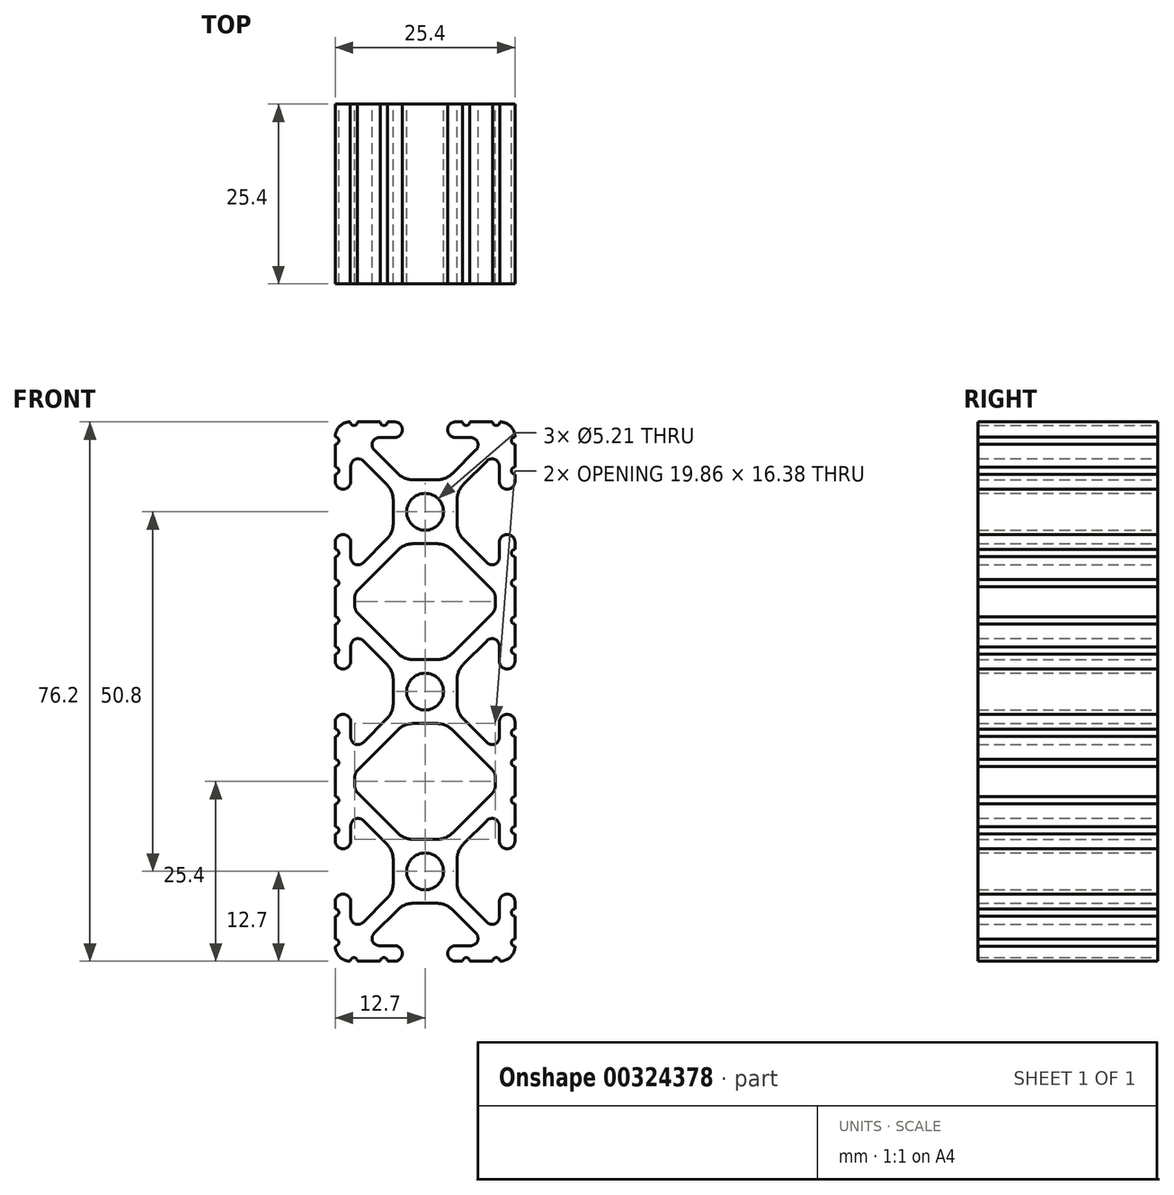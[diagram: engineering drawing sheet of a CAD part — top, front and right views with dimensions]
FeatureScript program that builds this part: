
annotation { "Feature Type Name" : "Feature", "Feature Type Description" : "" }
export const myFeature = defineFeature(function(context is Context, id is Id, definition is map)
    precondition{}
    {
        {
            var Q0;
            Q0=qCreatedBy(makeId("Front.planeOp"),FACE);
            var sketch = newSketch(context, id + "F0", { "sketchPlane" : qUnion([Q0])});
            skArc(sketch, "E0", {"start": v(2.6, 25.4) * mm, "mid": v(0, 28) * mm, "end": v(-2.6, 25.4) * mm});
            skArc(sketch, "E1", {"start": v(-2.6, 25.4) * mm, "mid": v(0, 22.8) * mm, "end": v(2.6, 25.4) * mm});
            skArc(sketch, "E2", {"start": v(-10.57, 38.1) * mm, "mid": v(-10.06, 37.6) * mm, "end": v(-9.55, 38.1) * mm});
            skArc(sketch, "E3", {"start": v(-10.57, 38.1) * mm, "mid": v(-12.08, 37.48) * mm, "end": v(-12.7, 35.97) * mm});
            skArc(sketch, "E4", {"start": v(-12.7, 34.95) * mm, "mid": v(-12.2, 35.46) * mm, "end": v(-12.7, 35.97) * mm});
            skLineSegment(sketch, "E5", {"start": v(-12.7, 34.95) * mm, "end": v(-12.7, 31.72) * mm});
            skArc(sketch, "E6", {"start": v(-12.7, 30.7) * mm, "mid": v(-12.2, 31.22) * mm, "end": v(-12.7, 31.72) * mm});
            skLineSegment(sketch, "E7", {"start": v(-12.7, 30.7) * mm, "end": v(-12.7, 29.7) * mm});
            skArc(sketch, "E8", {"start": v(-12.7, 29.7) * mm, "mid": v(-11.6, 28.6) * mm, "end": v(-10.5, 29.7) * mm});
            skLineSegment(sketch, "E9", {"start": v(-10.5, 29.7) * mm, "end": v(-10.5, 31.87) * mm});
            skArc(sketch, "E10", {"start": v(-8.76, 32.6) * mm, "mid": v(-9.86, 32.81) * mm, "end": v(-10.5, 31.87) * mm});
            skLineSegment(sketch, "E11", {"start": v(-8.76, 32.6) * mm, "end": v(-5.44, 29.28) * mm});
            skArc(sketch, "E12", {"start": v(-4.5, 27.03) * mm, "mid": v(-4.75, 28.25) * mm, "end": v(-5.44, 29.28) * mm});
            skLineSegment(sketch, "E13", {"start": v(-4.5, 27.03) * mm, "end": v(-4.5, 23.77) * mm});
            skArc(sketch, "E14", {"start": v(-5.44, 21.52) * mm, "mid": v(-4.75, 22.55) * mm, "end": v(-4.5, 23.77) * mm});
            skLineSegment(sketch, "E15", {"start": v(-5.44, 21.52) * mm, "end": v(-8.76, 18.2) * mm});
            skArc(sketch, "E16", {"start": v(-10.5, 18.93) * mm, "mid": v(-9.86, 17.99) * mm, "end": v(-8.76, 18.2) * mm});
            skLineSegment(sketch, "E17", {"start": v(-10.5, 18.93) * mm, "end": v(-10.5, 21.1) * mm});
            skArc(sketch, "E18", {"start": v(-10.5, 21.1) * mm, "mid": v(-11.6, 22.2) * mm, "end": v(-12.7, 21.1) * mm});
            skLineSegment(sketch, "E19", {"start": v(-12.7, 21.1) * mm, "end": v(-12.7, 20.1) * mm});
            skArc(sketch, "E20", {"start": v(-12.7, 19.08) * mm, "mid": v(-12.2, 19.58) * mm, "end": v(-12.7, 20.1) * mm});
            skLineSegment(sketch, "E21", {"start": v(-12.7, 19.08) * mm, "end": v(-12.7, 15.85) * mm});
            skArc(sketch, "E22", {"start": v(-12.7, 14.83) * mm, "mid": v(-12.2, 15.34) * mm, "end": v(-12.7, 15.85) * mm});
            skLineSegment(sketch, "E23", {"start": v(-12.7, 14.83) * mm, "end": v(-12.7, 10.57) * mm});
            skArc(sketch, "E24", {"start": v(-12.7, 9.55) * mm, "mid": v(-12.2, 10.06) * mm, "end": v(-12.7, 10.57) * mm});
            skLineSegment(sketch, "E25", {"start": v(-12.7, 9.55) * mm, "end": v(-12.7, 6.32) * mm});
            skArc(sketch, "E26", {"start": v(-12.7, 5.3) * mm, "mid": v(-12.2, 5.82) * mm, "end": v(-12.7, 6.32) * mm});
            skLineSegment(sketch, "E27", {"start": v(-12.7, 5.3) * mm, "end": v(-12.7, 4.3) * mm});
            skArc(sketch, "E28", {"start": v(-12.7, 4.3) * mm, "mid": v(-11.6, 3.2) * mm, "end": v(-10.5, 4.3) * mm});
            skLineSegment(sketch, "E29", {"start": v(-10.5, 4.3) * mm, "end": v(-10.5, 6.47) * mm});
            skArc(sketch, "E30", {"start": v(-8.76, 7.2) * mm, "mid": v(-9.86, 7.41) * mm, "end": v(-10.5, 6.47) * mm});
            skLineSegment(sketch, "E31", {"start": v(-8.76, 7.2) * mm, "end": v(-5.44, 3.88) * mm});
            skArc(sketch, "E32", {"start": v(-4.5, 1.63) * mm, "mid": v(-4.75, 2.85) * mm, "end": v(-5.44, 3.88) * mm});
            skLineSegment(sketch, "E33", {"start": v(-4.5, 1.63) * mm, "end": v(-4.5, -1.63) * mm});
            skArc(sketch, "E34", {"start": v(-5.44, -3.88) * mm, "mid": v(-4.75, -2.85) * mm, "end": v(-4.5, -1.63) * mm});
            skLineSegment(sketch, "E35", {"start": v(-5.44, -3.88) * mm, "end": v(-8.76, -7.2) * mm});
            skArc(sketch, "E36", {"start": v(-10.5, -6.47) * mm, "mid": v(-9.86, -7.41) * mm, "end": v(-8.76, -7.2) * mm});
            skLineSegment(sketch, "E37", {"start": v(-10.5, -6.47) * mm, "end": v(-10.5, -4.3) * mm});
            skArc(sketch, "E38", {"start": v(-10.5, -4.3) * mm, "mid": v(-11.6, -3.2) * mm, "end": v(-12.7, -4.3) * mm});
            skLineSegment(sketch, "E39", {"start": v(-12.7, -4.3) * mm, "end": v(-12.7, -5.3) * mm});
            skArc(sketch, "E40", {"start": v(-12.7, -6.32) * mm, "mid": v(-12.2, -5.82) * mm, "end": v(-12.7, -5.3) * mm});
            skLineSegment(sketch, "E41", {"start": v(-12.7, -6.32) * mm, "end": v(-12.7, -9.55) * mm});
            skArc(sketch, "E42", {"start": v(-12.7, -10.57) * mm, "mid": v(-12.2, -10.06) * mm, "end": v(-12.7, -9.55) * mm});
            skLineSegment(sketch, "E43", {"start": v(-12.7, -10.57) * mm, "end": v(-12.7, -14.83) * mm});
            skArc(sketch, "E44", {"start": v(-12.7, -15.85) * mm, "mid": v(-12.2, -15.34) * mm, "end": v(-12.7, -14.83) * mm});
            skLineSegment(sketch, "E45", {"start": v(-12.7, -15.85) * mm, "end": v(-12.7, -19.08) * mm});
            skArc(sketch, "E46", {"start": v(-12.7, -20.1) * mm, "mid": v(-12.2, -19.58) * mm, "end": v(-12.7, -19.08) * mm});
            skLineSegment(sketch, "E47", {"start": v(-12.7, -20.1) * mm, "end": v(-12.7, -21.1) * mm});
            skArc(sketch, "E48", {"start": v(-12.7, -21.1) * mm, "mid": v(-11.6, -22.2) * mm, "end": v(-10.5, -21.1) * mm});
            skLineSegment(sketch, "E49", {"start": v(-10.5, -21.1) * mm, "end": v(-10.5, -18.93) * mm});
            skArc(sketch, "E50", {"start": v(-8.76, -18.2) * mm, "mid": v(-9.86, -17.99) * mm, "end": v(-10.5, -18.93) * mm});
            skLineSegment(sketch, "E51", {"start": v(-8.76, -18.2) * mm, "end": v(-5.44, -21.52) * mm});
            skArc(sketch, "E52", {"start": v(-4.5, -23.77) * mm, "mid": v(-4.75, -22.55) * mm, "end": v(-5.44, -21.52) * mm});
            skLineSegment(sketch, "E53", {"start": v(-4.5, -23.77) * mm, "end": v(-4.5, -27.03) * mm});
            skArc(sketch, "E54", {"start": v(-5.44, -29.28) * mm, "mid": v(-4.75, -28.25) * mm, "end": v(-4.5, -27.03) * mm});
            skLineSegment(sketch, "E55", {"start": v(-5.44, -29.28) * mm, "end": v(-8.76, -32.6) * mm});
            skArc(sketch, "E56", {"start": v(-10.5, -31.87) * mm, "mid": v(-9.86, -32.81) * mm, "end": v(-8.76, -32.6) * mm});
            skLineSegment(sketch, "E57", {"start": v(-10.5, -31.87) * mm, "end": v(-10.5, -29.7) * mm});
            skArc(sketch, "E58", {"start": v(-10.5, -29.7) * mm, "mid": v(-11.6, -28.6) * mm, "end": v(-12.7, -29.7) * mm});
            skLineSegment(sketch, "E59", {"start": v(-12.7, -29.7) * mm, "end": v(-12.7, -30.7) * mm});
            skArc(sketch, "E60", {"start": v(-12.7, -31.72) * mm, "mid": v(-12.2, -31.22) * mm, "end": v(-12.7, -30.7) * mm});
            skLineSegment(sketch, "E61", {"start": v(-12.7, -31.72) * mm, "end": v(-12.7, -34.95) * mm});
            skArc(sketch, "E62", {"start": v(-12.7, -35.97) * mm, "mid": v(-12.2, -35.46) * mm, "end": v(-12.7, -34.95) * mm});
            skArc(sketch, "E63", {"start": v(-12.7, -35.97) * mm, "mid": v(-12.08, -37.48) * mm, "end": v(-10.57, -38.1) * mm});
            skArc(sketch, "E64", {"start": v(-9.55, -38.1) * mm, "mid": v(-10.06, -37.6) * mm, "end": v(-10.57, -38.1) * mm});
            skLineSegment(sketch, "E65", {"start": v(-9.55, -38.1) * mm, "end": v(-6.32, -38.1) * mm});
            skArc(sketch, "E66", {"start": v(-5.3, -38.1) * mm, "mid": v(-5.82, -37.6) * mm, "end": v(-6.32, -38.1) * mm});
            skLineSegment(sketch, "E67", {"start": v(-5.3, -38.1) * mm, "end": v(-4.3, -38.1) * mm});
            skArc(sketch, "E68", {"start": v(-4.3, -38.1) * mm, "mid": v(-3.2, -37) * mm, "end": v(-4.3, -35.9) * mm});
            skLineSegment(sketch, "E69", {"start": v(-4.3, -35.9) * mm, "end": v(-6.47, -35.9) * mm});
            skArc(sketch, "E70", {"start": v(-7.2, -34.16) * mm, "mid": v(-7.41, -35.26) * mm, "end": v(-6.47, -35.9) * mm});
            skLineSegment(sketch, "E71", {"start": v(-7.2, -34.16) * mm, "end": v(-3.88, -30.84) * mm});
            skArc(sketch, "E72", {"start": v(-1.63, -29.9) * mm, "mid": v(-2.85, -30.15) * mm, "end": v(-3.88, -30.84) * mm});
            skLineSegment(sketch, "E73", {"start": v(-1.63, -29.9) * mm, "end": v(1.63, -29.9) * mm});
            skArc(sketch, "E74", {"start": v(3.88, -30.84) * mm, "mid": v(2.85, -30.15) * mm, "end": v(1.63, -29.9) * mm});
            skLineSegment(sketch, "E75", {"start": v(3.88, -30.84) * mm, "end": v(7.2, -34.16) * mm});
            skArc(sketch, "E76", {"start": v(6.47, -35.9) * mm, "mid": v(7.41, -35.26) * mm, "end": v(7.2, -34.16) * mm});
            skLineSegment(sketch, "E77", {"start": v(6.47, -35.9) * mm, "end": v(4.3, -35.9) * mm});
            skArc(sketch, "E78", {"start": v(4.3, -35.9) * mm, "mid": v(3.2, -37) * mm, "end": v(4.3, -38.1) * mm});
            skLineSegment(sketch, "E79", {"start": v(4.3, -38.1) * mm, "end": v(5.3, -38.1) * mm});
            skArc(sketch, "E80", {"start": v(6.32, -38.1) * mm, "mid": v(5.82, -37.6) * mm, "end": v(5.3, -38.1) * mm});
            skLineSegment(sketch, "E81", {"start": v(6.32, -38.1) * mm, "end": v(9.55, -38.1) * mm});
            skArc(sketch, "E82", {"start": v(10.57, -38.1) * mm, "mid": v(10.06, -37.6) * mm, "end": v(9.55, -38.1) * mm});
            skArc(sketch, "E83", {"start": v(10.57, -38.1) * mm, "mid": v(12.08, -37.48) * mm, "end": v(12.7, -35.97) * mm});
            skArc(sketch, "E84", {"start": v(12.7, -34.95) * mm, "mid": v(12.2, -35.46) * mm, "end": v(12.7, -35.97) * mm});
            skLineSegment(sketch, "E85", {"start": v(12.7, -34.95) * mm, "end": v(12.7, -31.72) * mm});
            skArc(sketch, "E86", {"start": v(12.7, -30.7) * mm, "mid": v(12.2, -31.22) * mm, "end": v(12.7, -31.72) * mm});
            skLineSegment(sketch, "E87", {"start": v(12.7, -30.7) * mm, "end": v(12.7, -29.7) * mm});
            skArc(sketch, "E88", {"start": v(12.7, -29.7) * mm, "mid": v(11.6, -28.6) * mm, "end": v(10.5, -29.7) * mm});
            skLineSegment(sketch, "E89", {"start": v(10.5, -29.7) * mm, "end": v(10.5, -31.87) * mm});
            skArc(sketch, "E90", {"start": v(8.76, -32.6) * mm, "mid": v(9.86, -32.81) * mm, "end": v(10.5, -31.87) * mm});
            skLineSegment(sketch, "E91", {"start": v(8.76, -32.6) * mm, "end": v(5.44, -29.28) * mm});
            skArc(sketch, "E92", {"start": v(4.5, -27.03) * mm, "mid": v(4.75, -28.25) * mm, "end": v(5.44, -29.28) * mm});
            skLineSegment(sketch, "E93", {"start": v(4.5, -27.03) * mm, "end": v(4.5, -23.77) * mm});
            skArc(sketch, "E94", {"start": v(5.44, -21.52) * mm, "mid": v(4.75, -22.55) * mm, "end": v(4.5, -23.77) * mm});
            skLineSegment(sketch, "E95", {"start": v(5.44, -21.52) * mm, "end": v(8.76, -18.2) * mm});
            skArc(sketch, "E96", {"start": v(10.5, -18.93) * mm, "mid": v(9.86, -17.99) * mm, "end": v(8.76, -18.2) * mm});
            skLineSegment(sketch, "E97", {"start": v(10.5, -18.93) * mm, "end": v(10.5, -21.1) * mm});
            skArc(sketch, "E98", {"start": v(10.5, -21.1) * mm, "mid": v(11.6, -22.2) * mm, "end": v(12.7, -21.1) * mm});
            skLineSegment(sketch, "E99", {"start": v(12.7, -21.1) * mm, "end": v(12.7, -20.1) * mm});
            skArc(sketch, "E100", {"start": v(12.7, -19.08) * mm, "mid": v(12.2, -19.58) * mm, "end": v(12.7, -20.1) * mm});
            skLineSegment(sketch, "E101", {"start": v(12.7, -19.08) * mm, "end": v(12.7, -15.85) * mm});
            skArc(sketch, "E102", {"start": v(12.7, -14.83) * mm, "mid": v(12.2, -15.34) * mm, "end": v(12.7, -15.85) * mm});
            skLineSegment(sketch, "E103", {"start": v(12.7, -14.83) * mm, "end": v(12.7, -10.57) * mm});
            skArc(sketch, "E104", {"start": v(12.7, -9.55) * mm, "mid": v(12.2, -10.06) * mm, "end": v(12.7, -10.57) * mm});
            skLineSegment(sketch, "E105", {"start": v(12.7, -9.55) * mm, "end": v(12.7, -6.32) * mm});
            skArc(sketch, "E106", {"start": v(12.7, -5.3) * mm, "mid": v(12.2, -5.82) * mm, "end": v(12.7, -6.32) * mm});
            skLineSegment(sketch, "E107", {"start": v(12.7, -5.3) * mm, "end": v(12.7, -4.3) * mm});
            skArc(sketch, "E108", {"start": v(12.7, -4.3) * mm, "mid": v(11.6, -3.2) * mm, "end": v(10.5, -4.3) * mm});
            skLineSegment(sketch, "E109", {"start": v(10.5, -4.3) * mm, "end": v(10.5, -6.47) * mm});
            skArc(sketch, "E110", {"start": v(8.76, -7.2) * mm, "mid": v(9.86, -7.41) * mm, "end": v(10.5, -6.47) * mm});
            skLineSegment(sketch, "E111", {"start": v(8.76, -7.2) * mm, "end": v(5.44, -3.88) * mm});
            skArc(sketch, "E112", {"start": v(4.5, -1.63) * mm, "mid": v(4.75, -2.85) * mm, "end": v(5.44, -3.88) * mm});
            skLineSegment(sketch, "E113", {"start": v(4.5, -1.63) * mm, "end": v(4.5, 1.63) * mm});
            skArc(sketch, "E114", {"start": v(5.44, 3.88) * mm, "mid": v(4.75, 2.85) * mm, "end": v(4.5, 1.63) * mm});
            skLineSegment(sketch, "E115", {"start": v(5.44, 3.88) * mm, "end": v(8.76, 7.2) * mm});
            skArc(sketch, "E116", {"start": v(10.5, 6.47) * mm, "mid": v(9.86, 7.41) * mm, "end": v(8.76, 7.2) * mm});
            skLineSegment(sketch, "E117", {"start": v(10.5, 6.47) * mm, "end": v(10.5, 4.3) * mm});
            skArc(sketch, "E118", {"start": v(10.5, 4.3) * mm, "mid": v(11.6, 3.2) * mm, "end": v(12.7, 4.3) * mm});
            skLineSegment(sketch, "E119", {"start": v(12.7, 4.3) * mm, "end": v(12.7, 5.3) * mm});
            skArc(sketch, "E120", {"start": v(12.7, 6.32) * mm, "mid": v(12.2, 5.82) * mm, "end": v(12.7, 5.3) * mm});
            skLineSegment(sketch, "E121", {"start": v(12.7, 6.32) * mm, "end": v(12.7, 9.55) * mm});
            skArc(sketch, "E122", {"start": v(12.7, 10.57) * mm, "mid": v(12.2, 10.06) * mm, "end": v(12.7, 9.55) * mm});
            skLineSegment(sketch, "E123", {"start": v(12.7, 10.57) * mm, "end": v(12.7, 14.83) * mm});
            skArc(sketch, "E124", {"start": v(12.7, 15.85) * mm, "mid": v(12.2, 15.34) * mm, "end": v(12.7, 14.83) * mm});
            skLineSegment(sketch, "E125", {"start": v(12.7, 15.85) * mm, "end": v(12.7, 19.08) * mm});
            skArc(sketch, "E126", {"start": v(12.7, 20.1) * mm, "mid": v(12.2, 19.58) * mm, "end": v(12.7, 19.08) * mm});
            skLineSegment(sketch, "E127", {"start": v(12.7, 20.1) * mm, "end": v(12.7, 21.1) * mm});
            skArc(sketch, "E128", {"start": v(12.7, 21.1) * mm, "mid": v(11.6, 22.2) * mm, "end": v(10.5, 21.1) * mm});
            skLineSegment(sketch, "E129", {"start": v(10.5, 21.1) * mm, "end": v(10.5, 18.93) * mm});
            skArc(sketch, "E130", {"start": v(8.76, 18.2) * mm, "mid": v(9.86, 17.99) * mm, "end": v(10.5, 18.93) * mm});
            skLineSegment(sketch, "E131", {"start": v(8.76, 18.2) * mm, "end": v(5.44, 21.52) * mm});
            skArc(sketch, "E132", {"start": v(4.5, 23.77) * mm, "mid": v(4.75, 22.55) * mm, "end": v(5.44, 21.52) * mm});
            skLineSegment(sketch, "E133", {"start": v(4.5, 23.77) * mm, "end": v(4.5, 27.03) * mm});
            skArc(sketch, "E134", {"start": v(5.44, 29.28) * mm, "mid": v(4.75, 28.25) * mm, "end": v(4.5, 27.03) * mm});
            skLineSegment(sketch, "E135", {"start": v(5.44, 29.28) * mm, "end": v(8.76, 32.6) * mm});
            skArc(sketch, "E136", {"start": v(10.5, 31.87) * mm, "mid": v(9.86, 32.81) * mm, "end": v(8.76, 32.6) * mm});
            skLineSegment(sketch, "E137", {"start": v(10.5, 31.87) * mm, "end": v(10.5, 29.7) * mm});
            skArc(sketch, "E138", {"start": v(10.5, 29.7) * mm, "mid": v(11.6, 28.6) * mm, "end": v(12.7, 29.7) * mm});
            skLineSegment(sketch, "E139", {"start": v(12.7, 29.7) * mm, "end": v(12.7, 30.7) * mm});
            skArc(sketch, "E140", {"start": v(12.7, 31.72) * mm, "mid": v(12.2, 31.22) * mm, "end": v(12.7, 30.7) * mm});
            skLineSegment(sketch, "E141", {"start": v(12.7, 31.72) * mm, "end": v(12.7, 34.95) * mm});
            skArc(sketch, "E142", {"start": v(12.7, 35.97) * mm, "mid": v(12.2, 35.46) * mm, "end": v(12.7, 34.95) * mm});
            skArc(sketch, "E143", {"start": v(12.7, 35.97) * mm, "mid": v(12.08, 37.48) * mm, "end": v(10.57, 38.1) * mm});
            skArc(sketch, "E144", {"start": v(9.55, 38.1) * mm, "mid": v(10.06, 37.6) * mm, "end": v(10.57, 38.1) * mm});
            skLineSegment(sketch, "E145", {"start": v(9.55, 38.1) * mm, "end": v(6.32, 38.1) * mm});
            skArc(sketch, "E146", {"start": v(5.3, 38.1) * mm, "mid": v(5.82, 37.6) * mm, "end": v(6.32, 38.1) * mm});
            skLineSegment(sketch, "E147", {"start": v(5.3, 38.1) * mm, "end": v(4.3, 38.1) * mm});
            skArc(sketch, "E148", {"start": v(4.3, 38.1) * mm, "mid": v(3.2, 37) * mm, "end": v(4.3, 35.9) * mm});
            skLineSegment(sketch, "E149", {"start": v(4.3, 35.9) * mm, "end": v(6.47, 35.9) * mm});
            skArc(sketch, "E150", {"start": v(7.2, 34.16) * mm, "mid": v(7.41, 35.26) * mm, "end": v(6.47, 35.9) * mm});
            skLineSegment(sketch, "E151", {"start": v(7.2, 34.16) * mm, "end": v(3.88, 30.84) * mm});
            skArc(sketch, "E152", {"start": v(1.63, 29.9) * mm, "mid": v(2.85, 30.15) * mm, "end": v(3.88, 30.84) * mm});
            skLineSegment(sketch, "E153", {"start": v(1.63, 29.9) * mm, "end": v(-1.63, 29.9) * mm});
            skArc(sketch, "E154", {"start": v(-3.88, 30.84) * mm, "mid": v(-2.85, 30.15) * mm, "end": v(-1.63, 29.9) * mm});
            skLineSegment(sketch, "E155", {"start": v(-3.88, 30.84) * mm, "end": v(-7.2, 34.16) * mm});
            skArc(sketch, "E156", {"start": v(-6.47, 35.9) * mm, "mid": v(-7.41, 35.26) * mm, "end": v(-7.2, 34.16) * mm});
            skLineSegment(sketch, "E157", {"start": v(-6.47, 35.9) * mm, "end": v(-4.3, 35.9) * mm});
            skArc(sketch, "E158", {"start": v(-4.3, 35.9) * mm, "mid": v(-3.2, 37) * mm, "end": v(-4.3, 38.1) * mm});
            skLineSegment(sketch, "E159", {"start": v(-4.3, 38.1) * mm, "end": v(-5.3, 38.1) * mm});
            skArc(sketch, "E160", {"start": v(-6.32, 38.1) * mm, "mid": v(-5.82, 37.6) * mm, "end": v(-5.3, 38.1) * mm});
            skLineSegment(sketch, "E161", {"start": v(-6.32, 38.1) * mm, "end": v(-9.55, 38.1) * mm});
            skArc(sketch, "E162", {"start": v(2.6, 0) * mm, "mid": v(0, 2.6) * mm, "end": v(-2.6, 0) * mm});
            skArc(sketch, "E163", {"start": v(-2.6, 0) * mm, "mid": v(0, -2.6) * mm, "end": v(2.6, 0) * mm});
            skArc(sketch, "E164", {"start": v(2.6, -25.4) * mm, "mid": v(0, -22.8) * mm, "end": v(-2.6, -25.4) * mm});
            skArc(sketch, "E165", {"start": v(-2.6, -25.4) * mm, "mid": v(0, -28) * mm, "end": v(2.6, -25.4) * mm});
            skLineSegment(sketch, "E166", {"start": v(-3.88, -5.44) * mm, "end": v(-9.47, -11.03) * mm});
            skArc(sketch, "E167", {"start": v(-1.63, -4.5) * mm, "mid": v(-2.85, -4.75) * mm, "end": v(-3.88, -5.44) * mm});
            skLineSegment(sketch, "E168", {"start": v(1.63, -4.5) * mm, "end": v(-1.63, -4.5) * mm});
            skArc(sketch, "E169", {"start": v(3.88, -5.44) * mm, "mid": v(2.85, -4.75) * mm, "end": v(1.63, -4.5) * mm});
            skLineSegment(sketch, "E170", {"start": v(9.47, -11.03) * mm, "end": v(3.88, -5.44) * mm});
            skArc(sketch, "E171", {"start": v(9.93, -12.15) * mm, "mid": v(9.81, -11.54) * mm, "end": v(9.47, -11.03) * mm});
            skLineSegment(sketch, "E172", {"start": v(9.93, -13.25) * mm, "end": v(9.93, -12.15) * mm});
            skArc(sketch, "E173", {"start": v(9.47, -14.37) * mm, "mid": v(9.81, -13.86) * mm, "end": v(9.93, -13.25) * mm});
            skLineSegment(sketch, "E174", {"start": v(3.88, -19.96) * mm, "end": v(9.47, -14.37) * mm});
            skArc(sketch, "E175", {"start": v(1.63, -20.9) * mm, "mid": v(2.85, -20.65) * mm, "end": v(3.88, -19.96) * mm});
            skLineSegment(sketch, "E176", {"start": v(-1.63, -20.9) * mm, "end": v(1.63, -20.9) * mm});
            skArc(sketch, "E177", {"start": v(-3.88, -19.96) * mm, "mid": v(-2.85, -20.65) * mm, "end": v(-1.63, -20.9) * mm});
            skLineSegment(sketch, "E178", {"start": v(-9.47, -14.37) * mm, "end": v(-3.88, -19.96) * mm});
            skArc(sketch, "E179", {"start": v(-9.93, -13.25) * mm, "mid": v(-9.81, -13.86) * mm, "end": v(-9.47, -14.37) * mm});
            skLineSegment(sketch, "E180", {"start": v(-9.93, -12.15) * mm, "end": v(-9.93, -13.25) * mm});
            skArc(sketch, "E181", {"start": v(-9.47, -11.03) * mm, "mid": v(-9.81, -11.54) * mm, "end": v(-9.93, -12.15) * mm});
            skLineSegment(sketch, "E182", {"start": v(-3.88, 19.96) * mm, "end": v(-9.47, 14.37) * mm});
            skArc(sketch, "E183", {"start": v(-1.63, 20.9) * mm, "mid": v(-2.85, 20.65) * mm, "end": v(-3.88, 19.96) * mm});
            skLineSegment(sketch, "E184", {"start": v(1.63, 20.9) * mm, "end": v(-1.63, 20.9) * mm});
            skArc(sketch, "E185", {"start": v(3.88, 19.96) * mm, "mid": v(2.85, 20.65) * mm, "end": v(1.63, 20.9) * mm});
            skLineSegment(sketch, "E186", {"start": v(9.47, 14.37) * mm, "end": v(3.88, 19.96) * mm});
            skArc(sketch, "E187", {"start": v(9.93, 13.25) * mm, "mid": v(9.81, 13.86) * mm, "end": v(9.47, 14.37) * mm});
            skLineSegment(sketch, "E188", {"start": v(9.93, 12.15) * mm, "end": v(9.93, 13.25) * mm});
            skArc(sketch, "E189", {"start": v(9.47, 11.03) * mm, "mid": v(9.81, 11.54) * mm, "end": v(9.93, 12.15) * mm});
            skLineSegment(sketch, "E190", {"start": v(3.88, 5.44) * mm, "end": v(9.47, 11.03) * mm});
            skArc(sketch, "E191", {"start": v(1.63, 4.5) * mm, "mid": v(2.85, 4.75) * mm, "end": v(3.88, 5.44) * mm});
            skLineSegment(sketch, "E192", {"start": v(-1.63, 4.5) * mm, "end": v(1.63, 4.5) * mm});
            skArc(sketch, "E193", {"start": v(-3.88, 5.44) * mm, "mid": v(-2.85, 4.75) * mm, "end": v(-1.63, 4.5) * mm});
            skLineSegment(sketch, "E194", {"start": v(-9.47, 11.03) * mm, "end": v(-3.88, 5.44) * mm});
            skArc(sketch, "E195", {"start": v(-9.93, 12.15) * mm, "mid": v(-9.81, 11.54) * mm, "end": v(-9.47, 11.03) * mm});
            skLineSegment(sketch, "E196", {"start": v(-9.93, 13.25) * mm, "end": v(-9.93, 12.15) * mm});
            skArc(sketch, "E197", {"start": v(-9.47, 14.37) * mm, "mid": v(-9.81, 13.86) * mm, "end": v(-9.93, 13.25) * mm});
            skSolve(sketch);
        }
        {
            var Q0;
            Q0=makeQuery(id+"F0.imprint","IMPRINT",FACE,{"disambiguationData":[TD([[makeQuery(id+"F0.imprint","IMPRINT",EDGE,{"derivedFrom":sQuery(id+"F0.wireOp",EDGE,"E0")}),-1.0]])]});
            extrude(context, id + "F1", {"entities" : qUnion([Q0]), "depth" : 25.4 * mm});
        }
    });
